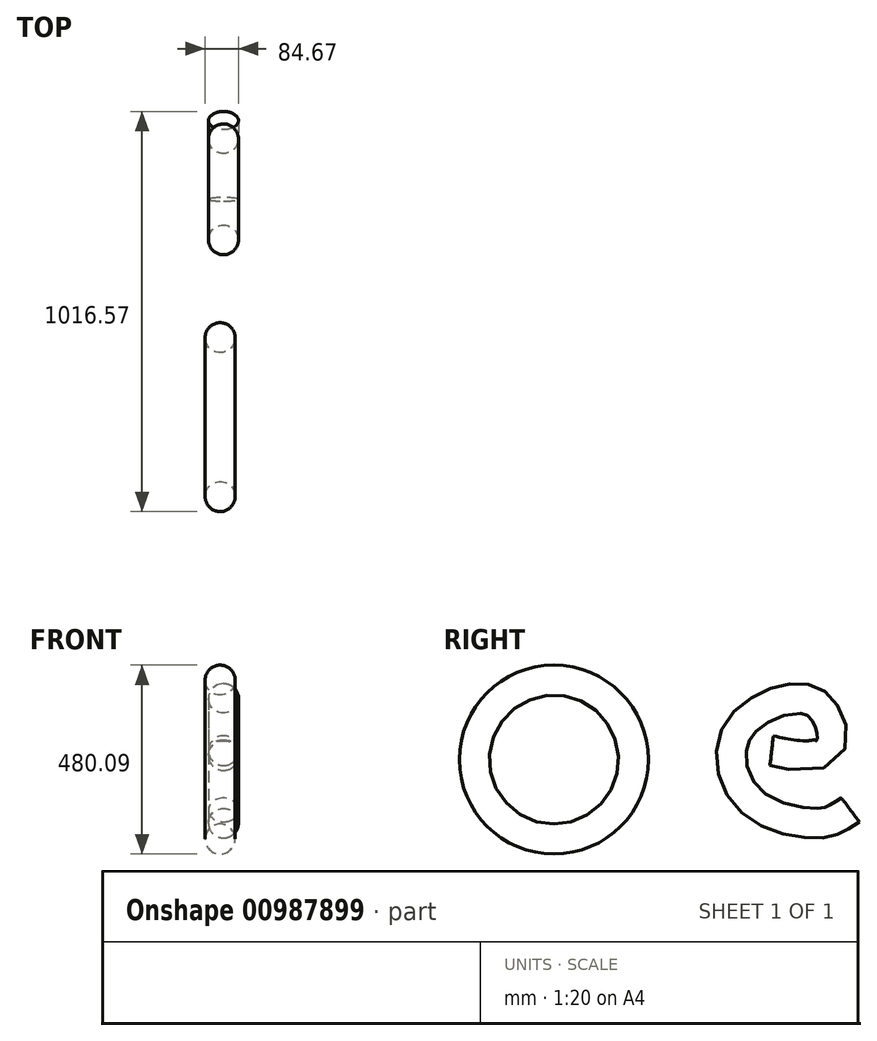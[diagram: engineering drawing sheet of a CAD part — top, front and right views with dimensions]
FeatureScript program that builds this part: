
annotation { "Feature Type Name" : "Feature", "Feature Type Description" : "" }
export const myFeature = defineFeature(function(context is Context, id is Id, definition is map)
    precondition{}
    {
        {
            var Q0;
            Q0=qCreatedBy(makeId("Front.planeOp"),FACE);
            var sketch = newSketch(context, id + "F0", { "sketchPlane" : qUnion([Q0])});
            skCircle(sketch, "E0", {"center": v(0, 0) * mm, "radius": 38.1 * mm});
            skLineSegment(sketch, "E1", {"start": v(0, -201.94) * mm, "end": v(60.6, -201.94) * mm});
            skLineSegment(sketch, "E2", {"start": v(60.6, -201.94) * mm, "end": v(-76.8, -201.94) * mm});
            skSolve(sketch);
        }
        {
            var Q0;
            Q0 = qSketchRegion(id + "F0", true);
            var Q1;
            Q1=sQuery(id+"F0.wireOp",EDGE,"E2");
            revolve(context, id + "F1", {"surfaceOperationType" : NewSurfaceOperationType.NEW, "entities" : qUnion([Q0]), "axis" : qUnion([Q1]), "revolveType" : RevolveType.FULL});
        }
        {
            var Q0;
            Q0=qCreatedBy(makeId("Right.planeOp"),FACE);
            cPlane(context, id + "F2", {"entities" : qUnion([Q0]), "cplaneType" : CPlaneType.OFFSET, "offset" : 254 * mm, "width" : 152.4 * mm, "height" : 152.4 * mm});
        }
        {
            var Q0;
            Q0=qCreatedBy(id+"F2.planeOp",FACE);
            var sketch = newSketch(context, id + "F3", { "sketchPlane" : qUnion([Q0])});
            skFitSpline(sketch, "E3", {"points": [v(-52.44, -190.37) * mm, v(99.25, -88.7) * mm, v(5.24, -35.45) * mm, v(-152.5, -133.89) * mm, v(-105.7, -321.08) * mm, v(86.34, -372.72) * mm, v(155.73, -338.84) * mm], "startDerivative": vector(3091, -766.14) * mm, "endDerivative": vector(803.91, 465.42) * mm});
            skSolve(sketch);
        }
        {
            var Q0;
            Q0=qCreatedBy(makeId("Front.planeOp"),FACE);
            var sketch = newSketch(context, id + "F4", { "sketchPlane" : qUnion([Q0])});
            skCircle(sketch, "E4", {"center": v(254.85, -189.25) * mm, "radius": 38.1 * mm});
            skSolve(sketch);
        }
        {
            var Q0;
            Q0=makeQuery(id+"F4.imprint","IMPRINT",FACE,{"disambiguationData":[TD([[makeQuery(id+"F4.imprint","IMPRINT",EDGE,{"derivedFrom":sQuery(id+"F4.wireOp",EDGE,"E4")}),1.0]])]});
            var Q1;
            Q1=sQuery(id+"F3.wireOp",EDGE,"E3");
            sweep(context, id + "F5", {"profiles" : qUnion([Q0]), "path" : qUnion([Q1])});
        }
        {
            var Q0;
            Q0=makeQuery(id+"F5.opSweep","SWEPT_BODY",BODY,{"disambiguationData":[OSD([sQuery(id+"F3.wireOp",EDGE,"E3"),sQuery(id+"F4.wireOp",EDGE,"E4")])]});
            transform(context, id + "F6", {"entities" : qUnion([Q0]), "transformType" : TransformType.TRANSLATION_3D, "dx" : -246.38 * mm, "dy" : 604.52 * mm, "dz" : 0 * mm, "makeCopy" : false});
        }
    });
